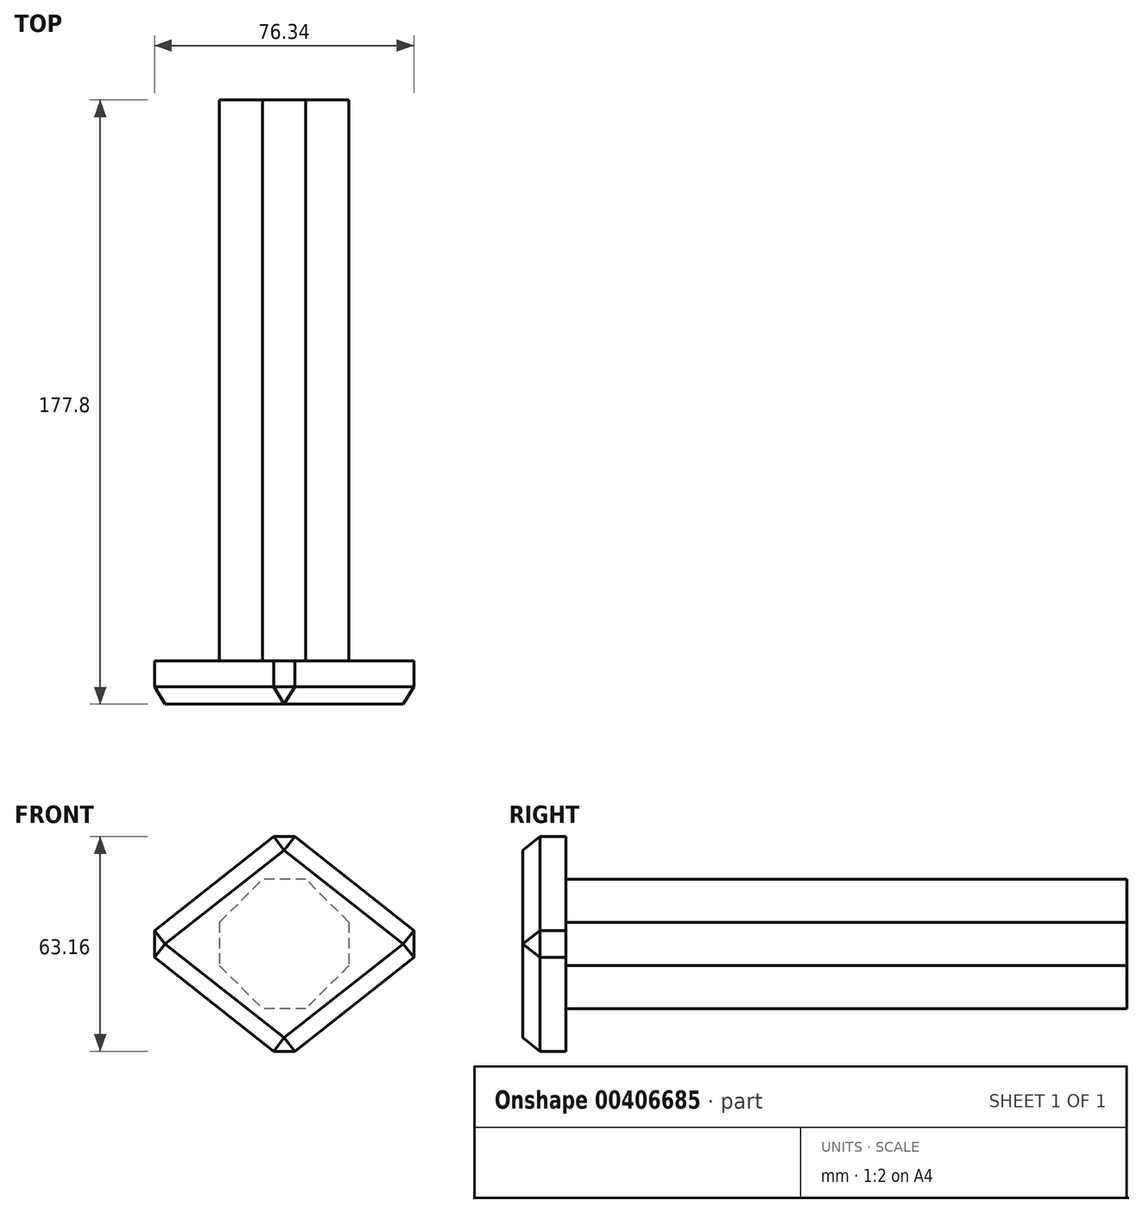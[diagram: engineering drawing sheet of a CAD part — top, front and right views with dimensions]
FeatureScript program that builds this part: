
annotation { "Feature Type Name" : "Feature", "Feature Type Description" : "" }
export const myFeature = defineFeature(function(context is Context, id is Id, definition is map)
    precondition{}
    {
        {
            var Q0;
            Q0=qCreatedBy(makeId("Front.planeOp"),FACE);
            var sketch = newSketch(context, id + "F0", { "sketchPlane" : qUnion([Q0])});
            skLineSegment(sketch, "E0.bottom", {"start": v(0, 0) * mm, "end": v(-38.1, 0) * mm});
            skLineSegment(sketch, "E0.top", {"start": v(0, -38.1) * mm, "end": v(-38.1, -38.1) * mm});
            skLineSegment(sketch, "E0.left", {"start": v(0, 0) * mm, "end": v(0, -38.1) * mm});
            skLineSegment(sketch, "E0.right", {"start": v(-38.1, 0) * mm, "end": v(-38.1, -38.1) * mm});
            skSolve(sketch);
        }
        {
            var Q0;
            Q0 = qSketchRegion(id + "F0", true);
            extrude(context, id + "F1", {"entities" : qUnion([Q0]), "depth" : 38.1 * mm});
        }
        {
            var Q0;
            Q0=makeQuery(id+"F1.opExtrude","CAP_FACE",FACE,{"disambiguationData":[OSD([sQuery(id+"F0.wireOp",EDGE,"E0.bottom"),sQuery(id+"F0.wireOp",EDGE,"E0.top"),sQuery(id+"F0.wireOp",EDGE,"E0.left"),sQuery(id+"F0.wireOp",EDGE,"E0.right")])],"isStart":false});
            var sketch = newSketch(context, id + "F2", { "sketchPlane" : qUnion([Q0])});
            skLineSegment(sketch, "E1", {"start": v(-38.1, 0) * mm, "end": v(-62.28, -19.05) * mm});
            skPoint(sketch, "E1.endSnap0", {"position": v(0, -19.05) * mm});
            skLineSegment(sketch, "E2", {"start": v(-62.28, -19.05) * mm, "end": v(-38.1, -38.1) * mm});
            skLineSegment(sketch, "E3", {"start": v(-38.1, -38.1) * mm, "end": v(-19.05, -53.1) * mm});
            skLineSegment(sketch, "E4", {"start": v(-19.05, -53.1) * mm, "end": v(0, -38.1) * mm});
            skLineSegment(sketch, "E5", {"start": v(0, -38.1) * mm, "end": v(24.18, -19.05) * mm});
            skLineSegment(sketch, "E6", {"start": v(24.18, -19.05) * mm, "end": v(0, 0) * mm});
            skLineSegment(sketch, "E7", {"start": v(0, 0) * mm, "end": v(-19.05, 15) * mm});
            skLineSegment(sketch, "E8", {"start": v(-19.05, 15) * mm, "end": v(-38.1, 0) * mm});
            skSolve(sketch);
        }
        {
            var Q0;
            Q0 = qSketchRegion(id + "F2", true);
            extrude(context, id + "F3", {"entities" : qUnion([Q0]), "operationType" : NewBodyOperationType.ADD, "depth" : 12.7 * mm});
        }
        {
            var Q0;
            Q0=makeQuery(id+"F3.opExtrude","CAP_EDGE",EDGE,{"disambiguationData":[OSD([sQuery(id+"F2.wireOp",EDGE,"E1"),sQuery(id+"F2.wireOp",EDGE,"E8")])],"isStart":false});
            var Q1;
            Q1=makeQuery(id+"F3.opExtrude","CAP_EDGE",EDGE,{"disambiguationData":[OSD([sQuery(id+"F2.wireOp",EDGE,"E2"),sQuery(id+"F2.wireOp",EDGE,"E3")])],"isStart":false});
            var Q2;
            Q2=makeQuery(id+"F3.opExtrude","CAP_EDGE",EDGE,{"disambiguationData":[OSD([sQuery(id+"F2.wireOp",EDGE,"E4"),sQuery(id+"F2.wireOp",EDGE,"E5")])],"isStart":false});
            var Q3;
            Q3=makeQuery(id+"F3.opExtrude","CAP_EDGE",EDGE,{"disambiguationData":[OSD([sQuery(id+"F2.wireOp",EDGE,"E6"),sQuery(id+"F2.wireOp",EDGE,"E7")])],"isStart":false});
            var Q4;
            Q4=makeQuery(id+"F3.opExtrude","SWEPT_EDGE",EDGE,{"disambiguationData":[OSD([sQuery(id+"F2.wireOp",EDGE,"E1"),sQuery(id+"F2.wireOp",EDGE,"E2")])]});
            var Q5;
            Q5=makeQuery(id+"F3.opExtrude","SWEPT_EDGE",EDGE,{"disambiguationData":[OSD([sQuery(id+"F2.wireOp",EDGE,"E3"),sQuery(id+"F2.wireOp",EDGE,"E4")])]});
            var Q6;
            Q6=makeQuery(id+"F3.opExtrude","SWEPT_EDGE",EDGE,{"disambiguationData":[OSD([sQuery(id+"F2.wireOp",EDGE,"E5"),sQuery(id+"F2.wireOp",EDGE,"E6")])]});
            var Q7;
            Q7=makeQuery(id+"F3.opExtrude","SWEPT_EDGE",EDGE,{"disambiguationData":[OSD([sQuery(id+"F2.wireOp",EDGE,"E7"),sQuery(id+"F2.wireOp",EDGE,"E8")])]});
            chamfer(context, id + "F4", {"entities" : qUnion([Q0, Q1, Q2, Q3, Q4, Q5, Q6, Q7]), "width" : 5.08 * mm, "tangentPropagation" : true});
        }
        {
            var Q0;
            Q0=makeQuery(id+"F1.opExtrude","SWEPT_EDGE",EDGE,{"disambiguationData":[OSD([sQuery(id+"F0.wireOp",EDGE,"E0.top"),sQuery(id+"F0.wireOp",EDGE,"E0.right")])]});
            var Q1;
            Q1=makeQuery(id+"F1.opExtrude","SWEPT_EDGE",EDGE,{"disambiguationData":[OSD([sQuery(id+"F0.wireOp",EDGE,"E0.top"),sQuery(id+"F0.wireOp",EDGE,"E0.left")])]});
            var Q2;
            Q2=makeQuery(id+"F1.opExtrude","SWEPT_EDGE",EDGE,{"disambiguationData":[OSD([sQuery(id+"F0.wireOp",EDGE,"E0.bottom"),sQuery(id+"F0.wireOp",EDGE,"E0.left")])]});
            var Q3;
            Q3=makeQuery(id+"F1.opExtrude","SWEPT_EDGE",EDGE,{"disambiguationData":[OSD([sQuery(id+"F0.wireOp",EDGE,"E0.bottom"),sQuery(id+"F0.wireOp",EDGE,"E0.right")])]});
            chamfer(context, id + "F5", {"entities" : qUnion([Q0, Q1, Q2, Q3]), "width" : 12.7 * mm, "tangentPropagation" : true});
        }
        {
            var Q0;
            Q0=makeQuery(id+"F1.opExtrude","CAP_FACE",FACE,{"disambiguationData":[OSD([sQuery(id+"F0.wireOp",EDGE,"E0.bottom"),sQuery(id+"F0.wireOp",EDGE,"E0.top"),sQuery(id+"F0.wireOp",EDGE,"E0.left"),sQuery(id+"F0.wireOp",EDGE,"E0.right")])],"isStart":true});
            var sketch = newSketch(context, id + "F6", { "sketchPlane" : qUnion([Q0])});
            skLineSegment(sketch, "E9", {"start": v(25.4, -38.1) * mm, "end": v(12.7, -38.1) * mm});
            skLineSegment(sketch, "E10", {"start": v(12.7, -38.1) * mm, "end": v(0, -25.4) * mm});
            skLineSegment(sketch, "E11", {"start": v(0, -25.4) * mm, "end": v(0, -12.7) * mm});
            skLineSegment(sketch, "E12", {"start": v(0, -12.7) * mm, "end": v(12.7, 0) * mm});
            skLineSegment(sketch, "E13", {"start": v(12.7, 0) * mm, "end": v(25.4, 0) * mm});
            skLineSegment(sketch, "E14", {"start": v(25.4, 0) * mm, "end": v(38.1, -12.7) * mm});
            skLineSegment(sketch, "E15", {"start": v(38.1, -12.7) * mm, "end": v(38.1, -25.4) * mm});
            skLineSegment(sketch, "E16", {"start": v(38.1, -25.4) * mm, "end": v(25.4, -38.1) * mm});
            skSolve(sketch);
        }
        {
            var Q0;
            Q0 = qSketchRegion(id + "F6", true);
            extrude(context, id + "F7", {"entities" : qUnion([Q0]), "operationType" : NewBodyOperationType.ADD, "depth" : 127 * mm});
        }
    });
